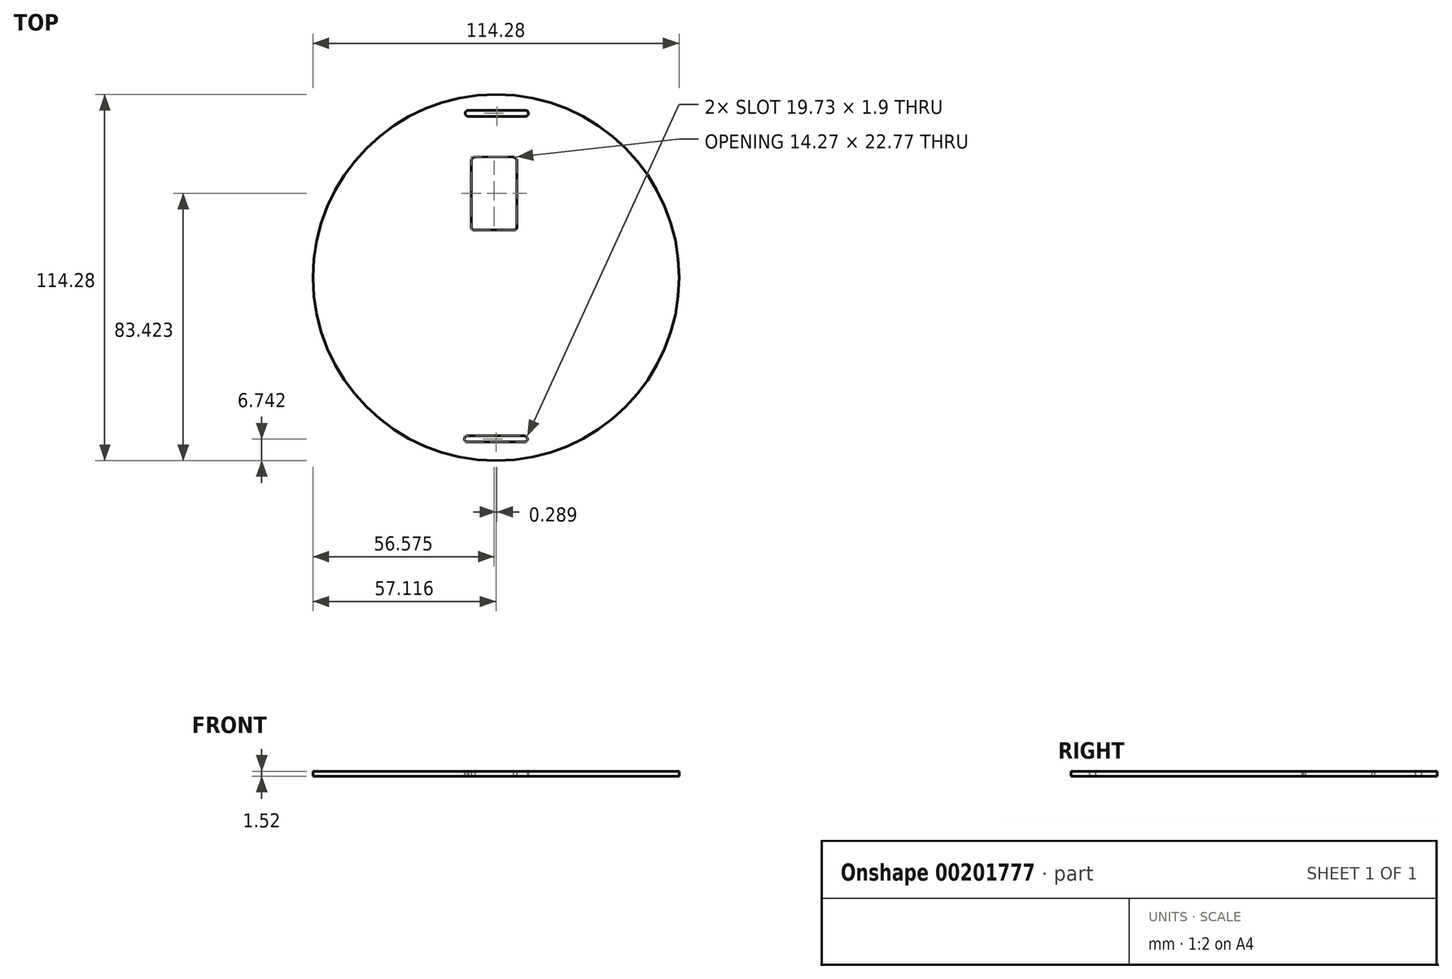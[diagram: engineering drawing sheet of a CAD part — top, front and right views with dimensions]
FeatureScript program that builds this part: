
annotation { "Feature Type Name" : "Feature", "Feature Type Description" : "" }
export const myFeature = defineFeature(function(context is Context, id is Id, definition is map)
    precondition{}
    {
        {
            var Q0;
            Q0=qCreatedBy(makeId("Top.planeOp"),FACE);
            var sketch = newSketch(context, id + "F0", { "sketchPlane" : qUnion([Q0])});
            skCircle(sketch, "E0", {"center": v(0, 0) * mm, "radius": 57.14 * mm});
            skLineSegment(sketch, "E1", {"start": v(0, -49.45) * mm, "end": v(8.9, -49.45) * mm});
            skLineSegment(sketch, "E2", {"start": v(8.9, -49.45) * mm, "end": v(0, -49.45) * mm});
            skLineSegment(sketch, "E3", {"start": v(0, -49.45) * mm, "end": v(-8.87, -49.45) * mm});
            skLineSegment(sketch, "E4", {"start": v(0, -51.35) * mm, "end": v(8.9, -51.35) * mm});
            skLineSegment(sketch, "E5", {"start": v(8.9, -51.35) * mm, "end": v(-8.94, -51.35) * mm});
            skArc(sketch, "E6", {"start": v(-8.87, -49.45) * mm, "mid": v(-9.89, -50.36) * mm, "end": v(-8.94, -51.35) * mm});
            skArc(sketch, "E7", {"start": v(8.9, -51.35) * mm, "mid": v(9.84, -50.4) * mm, "end": v(8.9, -49.45) * mm});
            skLineSegment(sketch, "E8", {"start": v(-1.4, 52.22) * mm, "end": v(9.18, 52.22) * mm});
            skLineSegment(sketch, "E9", {"start": v(9.18, 52.22) * mm, "end": v(-1.4, 52.22) * mm});
            skLineSegment(sketch, "E10", {"start": v(-1.4, 52.22) * mm, "end": v(-8.58, 52.22) * mm});
            skLineSegment(sketch, "E11", {"start": v(-1.4, 50.32) * mm, "end": v(9.18, 50.32) * mm});
            skLineSegment(sketch, "E12", {"start": v(9.18, 50.32) * mm, "end": v(-8.65, 50.32) * mm});
            skArc(sketch, "E13", {"start": v(-8.58, 52.22) * mm, "mid": v(-9.6, 51.3) * mm, "end": v(-8.65, 50.32) * mm});
            skArc(sketch, "E14", {"start": v(9.18, 50.32) * mm, "mid": v(10.13, 51.27) * mm, "end": v(9.18, 52.22) * mm});
            skLineSegment(sketch, "E15", {"start": v(-7.02, 14.9) * mm, "end": v(5.75, 14.9) * mm});
            skLineSegment(sketch, "E16", {"start": v(6.51, 15.4) * mm, "end": v(6.51, 36.7) * mm});
            skLineSegment(sketch, "E17", {"start": v(-7.7, 15.4) * mm, "end": v(-7.7, 36.44) * mm});
            skLineSegment(sketch, "E18", {"start": v(-6.63, 37.6) * mm, "end": v(5.33, 37.67) * mm});
            skArc(sketch, "E19", {"start": v(6.51, 36.7) * mm, "mid": v(6.04, 37.32) * mm, "end": v(5.33, 37.67) * mm});
            skLineSegment(sketch, "E20", {"start": v(-7.7, 36.44) * mm, "end": v(-7.7, 15.4) * mm});
            skLineSegment(sketch, "E21", {"start": v(6.51, 36.7) * mm, "end": v(6.51, 15.4) * mm});
            skLineSegment(sketch, "E22", {"start": v(5.75, 14.9) * mm, "end": v(-7.02, 14.9) * mm});
            skArc(sketch, "E23", {"start": v(-6.63, 37.6) * mm, "mid": v(-7.39, 37.23) * mm, "end": v(-7.7, 36.44) * mm});
            skArc(sketch, "E24", {"start": v(5.75, 14.9) * mm, "mid": v(6.43, 15.26) * mm, "end": v(6.51, 16.03) * mm});
            skArc(sketch, "E25", {"start": v(-7.7, 15.4) * mm, "mid": v(-7.44, 15.04) * mm, "end": v(-7.02, 14.9) * mm});
            skSolve(sketch);
        }
        {
            var Q0;
            Q0=makeQuery(id+"F0.imprint","IMPRINT",FACE,{"disambiguationData":[TD([[makeQuery(id+"F0.imprint","IMPRINT",EDGE,{"derivedFrom":sQuery(id+"F0.wireOp",EDGE,"E0")}),1.0]])]});
            extrude(context, id + "F1", {"entities" : qUnion([Q0]), "depth" : 1.52 * mm});
        }
    });
